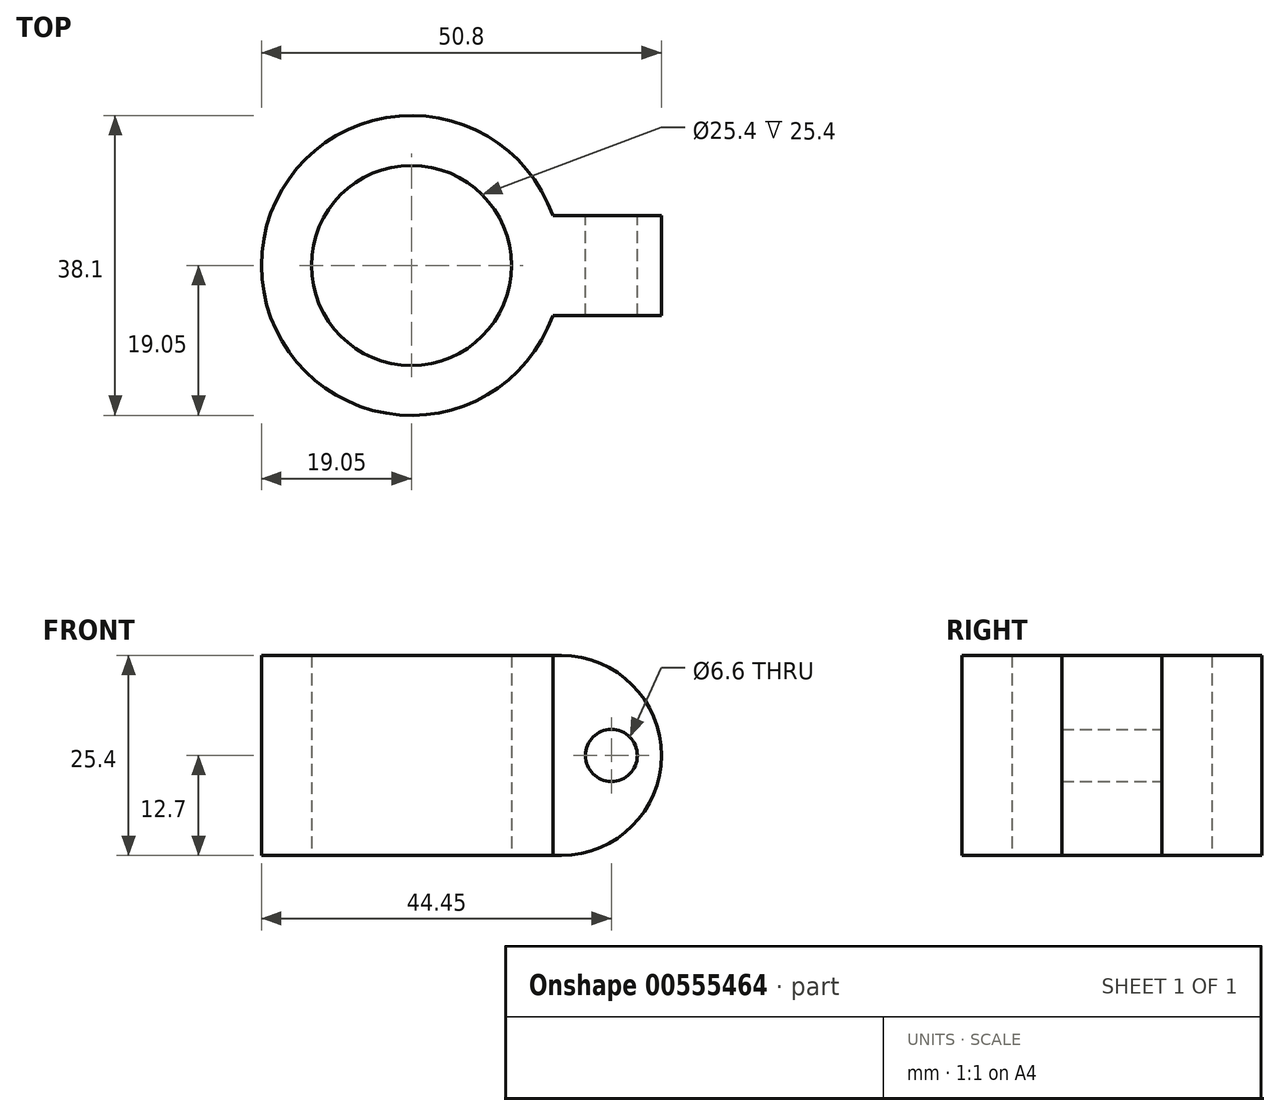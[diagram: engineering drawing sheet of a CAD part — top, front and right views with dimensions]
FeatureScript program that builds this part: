
annotation { "Feature Type Name" : "Feature", "Feature Type Description" : "" }
export const myFeature = defineFeature(function(context is Context, id is Id, definition is map)
    precondition{}
    {
        {
            var Q0;
            Q0=qCreatedBy(makeId("Front.planeOp"),FACE);
            var sketch = newSketch(context, id + "F0", { "sketchPlane" : qUnion([Q0])});
            skLineSegment(sketch, "E0.bottom", {"start": v(-12.7, 0) * mm, "end": v(-19.05, 0) * mm});
            skLineSegment(sketch, "E0.top", {"start": v(-12.7, 25.4) * mm, "end": v(-19.05, 25.4) * mm});
            skLineSegment(sketch, "E0.left", {"start": v(-12.7, 0) * mm, "end": v(-12.7, 25.4) * mm});
            skLineSegment(sketch, "E0.right", {"start": v(-19.05, 0) * mm, "end": v(-19.05, 25.4) * mm});
            skSolve(sketch);
        }
        {
            var Q0;
            Q0=qCreatedBy(makeId("Front.planeOp"),FACE);
            var sketch = newSketch(context, id + "F1", { "sketchPlane" : qUnion([Q0])});
            skLineSegment(sketch, "E1", {"start": v(0, -20.83) * mm, "end": v(0, 68.83) * mm});
            skSolve(sketch);
        }
        {
            var Q0;
            Q0=makeQuery(id+"F0.imprint","IMPRINT",FACE,{"disambiguationData":[TD([[makeQuery(id+"F0.imprint","IMPRINT",EDGE,{"derivedFrom":sQuery(id+"F0.wireOp",EDGE,"E0.bottom")}),-1.0]])]});
            var Q1;
            Q1=sQuery(id+"F1.wireOp",EDGE,"E1");
            revolve(context, id + "F2", {"entities" : qUnion([Q0]), "axis" : qUnion([Q1]), "revolveType" : RevolveType.FULL});
        }
        {
            var Q0;
            Q0=qCreatedBy(makeId("Front.planeOp"),FACE);
            var sketch = newSketch(context, id + "F3", { "sketchPlane" : qUnion([Q0])});
            skLineSegment(sketch, "E2.bottom", {"start": v(19.05, 25.4) * mm, "end": v(12.7, 25.4) * mm});
            skLineSegment(sketch, "E2.top", {"start": v(19.05, 0) * mm, "end": v(12.7, 0) * mm});
            skLineSegment(sketch, "E2.left", {"start": v(19.05, 25.4) * mm, "end": v(19.05, 0) * mm});
            skLineSegment(sketch, "E2.right", {"start": v(12.7, 25.4) * mm, "end": v(12.7, 0) * mm});
            skArc(sketch, "E3", {"start": v(19.05, 0) * mm, "mid": v(31.75, 12.7) * mm, "end": v(19.05, 25.4) * mm});
            skCircle(sketch, "E4", {"center": v(25.4, 12.7) * mm, "radius": 3.3 * mm});
            skSolve(sketch);
        }
        {
            var Q0;
            Q0=qSketchRegion(id+"F3",true);
            extrude(context, id + "F4", {"entities" : qUnion([Q0]), "operationType" : NewBodyOperationType.ADD, "depth" : 6.35 * mm, "offsetDistance" : 25.4 * mm, "hasSecondDirection" : true, "secondDirectionOppositeDirection" : true, "secondDirectionDepth" : 6.35 * mm});
        }
    });
